MODEL slx_3bae1924328a
CONFIG AbsTol = auto
CONFIG FixedStep = 0.01
CONFIG MaxStep = auto
CONFIG MinStep = auto
CONFIG RelTol = 1e-3
CONFIG SampleTimeConstraint = Unconstrained
CONFIG Solver = FixedStepDiscrete
CONFIG SolverMode = Auto
CONFIG SolverName = FixedStepDiscrete
CONFIG StartTime = 0.0
CONFIG StopTime = 10
BLOCK [Constant] Constant
  Value = 20
BLOCK [Constant] Constant2
  Value = 200
BLOCK [Logic] Logical Operator
  AllPortsSameDT = off
  OutDataTypeStr = boolean
  Ports = [2, 1]
BLOCK [Logic] Logical Operator1
  AllPortsSameDT = off
  OutDataTypeStr = boolean
  Ports = [2, 1]
BLOCK [Logic] Logical Operator2
  AllPortsSameDT = off
  Operator = OR
  OutDataTypeStr = boolean
  Ports = [2, 1]
BLOCK [Logic] Logical Operator3
  AllPortsSameDT = off
  OutDataTypeStr = boolean
  Ports = [2, 1]
BLOCK [RelationalOperator] Relational Operator
  InputSameDT = off
  Operator = >
  OutDataTypeStr = boolean
  Ports = [2, 1]
BLOCK [RelationalOperator] Relational Operator1
  InputSameDT = off
  Operator = <
  OutDataTypeStr = boolean
  Ports = [2, 1]
BLOCK [Scope] Scope
  NumInputPorts = 5
  Ports = [5]
  ScopeSpecificationString = Simulink.scopes.TimeScopeBlockCfg('CurrentConfiguration', extmgr.ConfigurationSet(extmgr.Configuration('Core','General UI',true),extmgr.Configuration('Core','Source UI',true),extmgr.Configuration('Sources','WiredSimulink',true,'DataLoggingSaveFormat','StructureWithTime','DataLoggingLimitDataPoints',true,'DataLoggingDecimation','1','DataLoggingDecimateData',true),extmgr.Configuration('Visuals','Tim...<+6411ch>
BLOCK [SubSystem] Signal Builder
  ClipboardFcn = sigbuilder_block('clipboard');
  CloseFcn = sigbuilder_block('close');
  ContinueFcn = sigbuilder_block('continue');
  CopyFcn = sigbuilder_block('copy');
  DeleteFcn = sigbuilder_block('delete');
  LoadFcn = sigbuilder_block('load');
  MaskHideContents = on
  ModelCloseFcn = sigbuilder_block('modelClose');
  NameChangeFcn = sigbuilder_block('namechange');
  OpenFcn = sigbuilder_block('open',[249.75 69 738 441.75 ]);
  PauseFcn = sigbuilder_block('pause');
  Ports = [0, 2]
  PreSaveFcn = sigbuilder_block('preSave');
  RequestExecContextInheritance = off
  StartFcn = sigbuilder_block('start');
  StopFcn = sigbuilder_block('stop');
  Tag = STV Subsys
  Variant = off
BLOCK [Demux] Signal Builder/Demux
  Outputs = 2
  Ports = [1, 2]
  Tag = STV Demux
BLOCK [FromWorkspace] Signal Builder/FromWs
  SampleTime = 0
  Tag = STV FromWs
  VariableName = tuvar
  ZeroCross = on
BLOCK [Outport] Signal Builder/IG_SW
  IconDisplay = Port number
  Tag = STV Outport
BLOCK [Outport] Signal Builder/WP_SW
  IconDisplay = Port number
  Port = 2
  Tag = STV Outport
BLOCK [SubSystem] Subsystem
  Ports = [2, 1]
  RequestExecContextInheritance = off
  Variant = off
BLOCK [Sum] Subsystem/Add
  InputSameDT = off
  OutDataTypeStr = Inherit: Inherit via internal rule
  Ports = [2, 1]
  SaturateOnIntegerOverflow = off
BLOCK [Inport] Subsystem/ClearReq
  IconDisplay = Port number
  Port = 2
BLOCK [Constant] Subsystem/Constant
  OutDataTypeStr = double
BLOCK [Constant] Subsystem/Constant1
  OutDataTypeStr = double
  Value = 0
BLOCK [Inport] Subsystem/CountUpReq
  IconDisplay = Port number
BLOCK [Outport] Subsystem/Counter
  IconDisplay = Port number
BLOCK [Switch] Subsystem/Switch
  Criteria = u2 ~= 0
  InputSameDT = off
  SaturateOnIntegerOverflow = off
BLOCK [Switch] Subsystem/Switch1
  Criteria = u2 ~= 0
  InputSameDT = off
  SaturateOnIntegerOverflow = off
BLOCK [UnitDelay] Subsystem/Unit Delay
  InputProcessing = Elements as channels (sample based)
  SampleTime = -1
BLOCK [UnitDelay] Subsystem/Unit Delay1
  InputProcessing = Elements as channels (sample based)
  SampleTime = -1
BLOCK [UnitDelay] Unit Delay
  InputProcessing = Elements as channels (sample based)
  SampleTime = -1
LINE Constant2:1 -> Relational Operator1:2
LINE Constant:1 -> Relational Operator:2
LINE Logical Operator1:1 -> Logical Operator2:2
LINE Logical Operator1:1 -> Scope:5
LINE Logical Operator1:1 -> Subsystem:2
LINE Logical Operator2:1 -> Logical Operator3:1
LINE Logical Operator3:1 -> Scope:4
LINE Logical Operator3:1 -> Subsystem:1
LINE Logical Operator:1 -> Logical Operator2:1
LINE Relational Operator1:1 -> Logical Operator3:2
LINE Relational Operator:1 -> Logical Operator1:2
LINE Signal Builder:1 -> Logical Operator1:1
LINE Signal Builder:1 -> Logical Operator:2
LINE Signal Builder:1 -> Scope:1
LINE Signal Builder:2 -> Logical Operator:1
LINE Signal Builder:2 -> Scope:2
LINE Subsystem/Add:1 -> Subsystem/Switch:1
LINE Subsystem/ClearReq:1 -> Subsystem/Switch1:2
LINE Subsystem/Constant1:1 -> Subsystem/Switch1:1
LINE Subsystem/Constant:1 -> Subsystem/Add:2
LINE Subsystem/CountUpReq:1 -> Subsystem/Switch:2
LINE Subsystem/Switch1:1 -> Subsystem/Switch:3
LINE Subsystem/Switch:1 -> Subsystem/Counter:1
LINE Subsystem/Switch:1 -> Subsystem/Unit Delay1:1
LINE Subsystem/Switch:1 -> Subsystem/Unit Delay:1
LINE Subsystem/Unit Delay1:1 -> Subsystem/Switch1:3
LINE Subsystem/Unit Delay:1 -> Subsystem/Add:1
LINE Subsystem:1 -> Scope:3
LINE Subsystem:1 -> Unit Delay:1
LINE Unit Delay:1 -> Relational Operator1:1
LINE Unit Delay:1 -> Relational Operator:1
